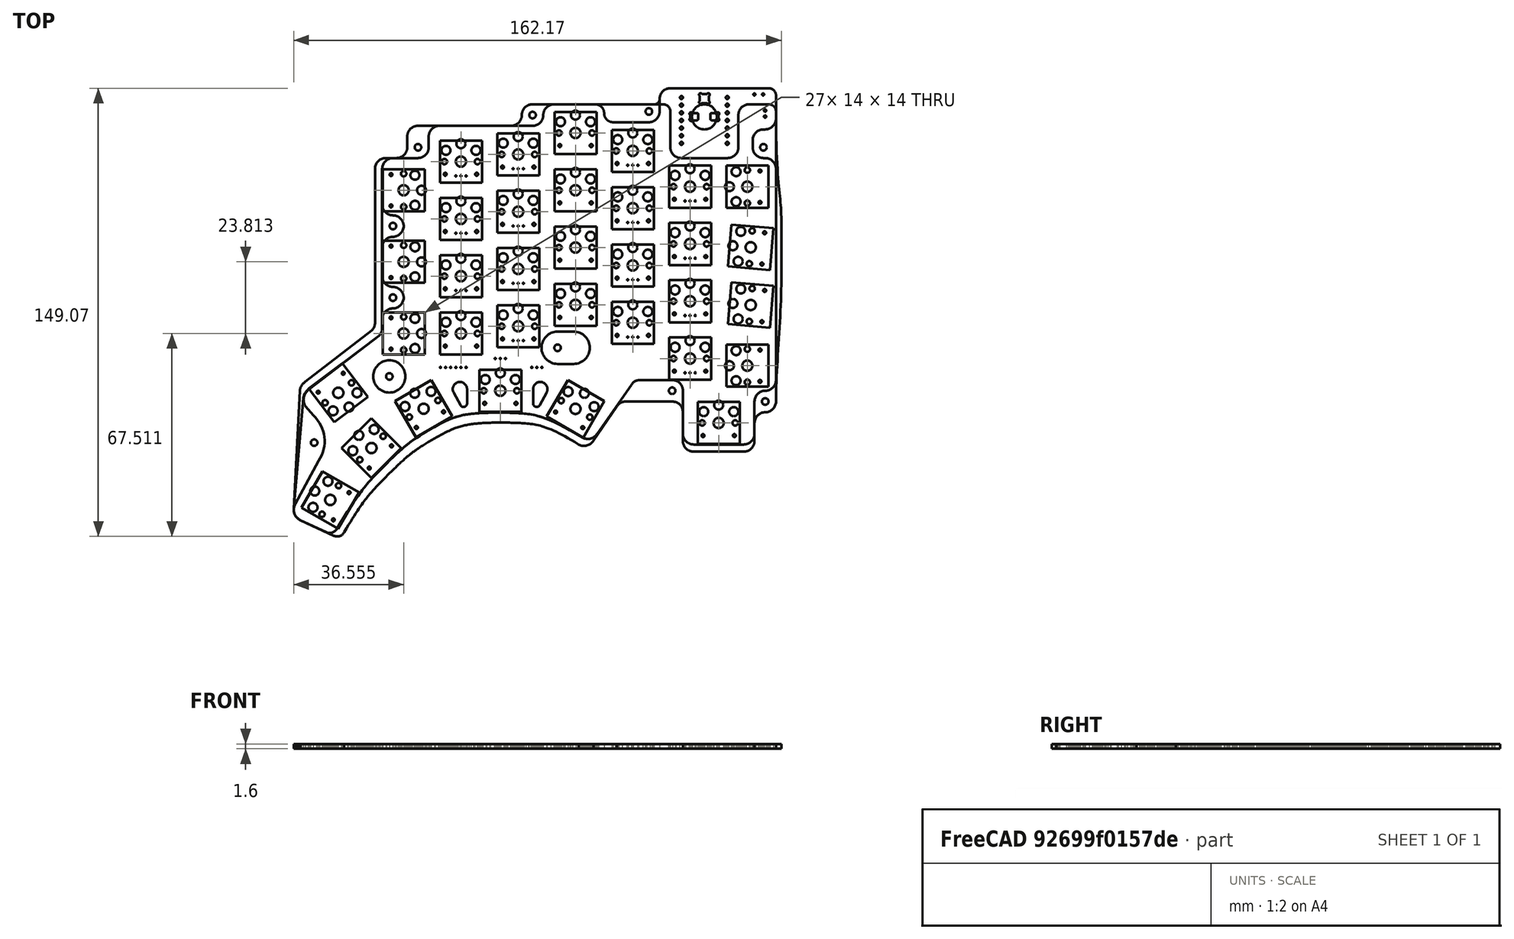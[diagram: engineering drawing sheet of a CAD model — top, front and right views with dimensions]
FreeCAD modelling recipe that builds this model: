
FCSTD DOCUMENT  (FreeCAD 0.20RUnknown)
Label: mykeeb_v7a3
License: All rights reserved
LicenseURL: http://en.wikipedia.org/wiki/All_rights_reserved
objects: App::Part×9, PartDesign::CoordinateSystem×3, Part::Feature×3, Sketcher::SketchObject×3
note: 9 computed .brp shape members not serialized (recipe doc carries the construction recipe); baked Part::Feature solids carry a one-line shape summary decoded from their .brp

FEATURE [PartDesign::CoordinateSystem] Local_CS_73e4
  AttacherType = Attacher::AttachEngine3D
  MapMode = 2
  Support = -> [X_Axis001]
FEATURE [Part::Feature] Pcb_73e4
  shape: bbox 160.4 x 147.9 x 1.6 mm, 455 faces (baked)
FEATURE [Sketcher::SketchObject] PCB_Sketch_73e4
  FullyConstrained = false
  sketch-geometry (120):
    g0: LineSegment StartX=214.313 StartY=-44.0531 StartZ=0 EndX=214.908 EndY=-44.0532 EndZ=0
    g1: LineSegment StartX=63.1589 StartY=-130.538 StartZ=0 EndX=86.4648 EndY=-112.659 EndZ=0
    g2: LineSegment StartX=218.48 StartY=-40.4812 StartZ=0 EndX=218.48 EndY=-32.7422 EndZ=0
    g3: LineSegment StartX=66.3691 StartY=-154.273 StartZ=0 EndX=58.6299 EndY=-168.63 EndZ=0
    g4: LineSegment StartX=159.033 StartY=-145.204 StartZ=0 EndX=170.339 EndY=-129.07 EndZ=0
    g5: LineSegment StartX=87.511 StartY=-92.8689 StartZ=0 EndX=87.511 EndY=-83.3438 EndZ=0
    g6: LineSegment StartX=60.2956 StartY=-173.994 StartZ=0 EndX=68.974 EndY=-178.03 EndZ=0
    g7: LineSegment StartX=216.099 StartY=-30.361 StartZ=0 EndX=183.356 EndY=-30.3609 EndZ=0
    g8: LineSegment StartX=191.095 StartY=-148.828 StartZ=0 EndX=207.764 EndY=-148.828 EndZ=0
    g9: LineSegment StartX=64.6194 StartY=-139.172 StartZ=0 EndX=62.0519 EndY=-136.234 EndZ=0
    g10: LineSegment StartX=218.48 StartY=-57.15 StartZ=0 EndX=218.48 EndY=-127.397 EndZ=0
    g11: LineSegment StartX=115.741 StartY=-130.425 StartZ=0 EndX=115.741 EndY=-135.187 EndZ=0
    g12: LineSegment StartX=187.524 StartY=-145.256 StartZ=0 EndX=187.524 EndY=-130.969 EndZ=0
    g13: LineSegment StartX=211.336 StartY=-145.256 StartZ=0 EndX=211.336 EndY=-134.541 EndZ=0
    g14: LineSegment StartX=87.511 StartY=-69.0563 StartZ=0 EndX=87.511 EndY=-57.15 EndZ=0
    g15: LineSegment StartX=99.4173 StartY=-53.5782 StartZ=0 EndX=91.0829 EndY=-53.5782 EndZ=0
    g16: LineSegment StartX=145.852 StartY=-122.039 StartZ=0 EndX=151.21 EndY=-122.039 EndZ=0
    g17: LineSegment StartX=137.717 StartY=-135.187 StartZ=0 EndX=137.717 EndY=-130.425 EndZ=0
    g18: LineSegment StartX=179.785 StartY=-38.1 StartZ=0 EndX=179.785 EndY=-33.9328 EndZ=0
    g19: LineSegment StartX=183.952 StartY=-127.397 StartZ=0 EndX=173.236 EndY=-127.397 EndZ=0
    g20: LineSegment StartX=106.561 StartY=-42.8625 StartZ=0 EndX=137.517 EndY=-42.8626 EndZ=0
    g21: LineSegment StartX=111.318 StartY=-131.65 StartZ=0 EndX=113.56 EndY=-135.848 EndZ=0
    g22: LineSegment StartX=210.741 StartY=-47.625 StartZ=0 EndX=210.741 EndY=-50.0063 EndZ=0
    g23: LineSegment StartX=214.313 StartY=-53.5782 StartZ=0 EndX=214.908 EndY=-53.5782 EndZ=0
    g24: LineSegment StartX=102.989 StartY=-50.0063 StartZ=0 EndX=102.989 EndY=-46.4344 EndZ=0
    g25: LineSegment StartX=164.307 StartY=-41.6719 StartZ=0 EndX=176.213 EndY=-41.6719 EndZ=0
    g26: LineSegment StartX=145.852 StartY=-111.324 StartZ=0 EndX=151.21 EndY=-111.324 EndZ=0
    g27: LineSegment StartX=144.661 StartY=-35.7187 StartZ=0 EndX=158.353 EndY=-35.7186 EndZ=0
    g28: LineSegment StartX=87.511 StartY=-107.156 StartZ=0 EndX=87.511 EndY=-110.133 EndZ=0
    g29: LineSegment StartX=139.899 StartY=-135.848 StartZ=0 EndX=142.14 EndY=-131.65 EndZ=0
    g30: BSplineCurve PolesCount=4 KnotsCount=2 Degree=3 IsPeriodic=0
    g31: BSplineCurve PolesCount=4 KnotsCount=2 Degree=3 IsPeriodic=0
    g32: BSplineCurve PolesCount=4 KnotsCount=2 Degree=3 IsPeriodic=0
    g33: BSplineCurve PolesCount=4 KnotsCount=2 Degree=3 IsPeriodic=0
    g34: BSplineCurve PolesCount=4 KnotsCount=2 Degree=3 IsPeriodic=0
    g35: BSplineCurve PolesCount=4 KnotsCount=2 Degree=3 IsPeriodic=0
    g36: BSplineCurve PolesCount=4 KnotsCount=2 Degree=3 IsPeriodic=0
    g37: ArcOfCircle CenterX=214.908 CenterY=-127.397 CenterZ=0 NormalX=0 NormalY=0 NormalZ=-1 AngleXU=3.14159 Radius=3.57183 StartAngle=0 EndAngle=1.57081
    g38: ArcOfCircle CenterX=183.356 CenterY=-33.9326 CenterZ=0 NormalX=0 NormalY=0 NormalZ=-1 AngleXU=-6.74926e-05 Radius=3.57168 StartAngle=0 EndAngle=1.57092
    g39: ArcOfCircle CenterX=138.908 CenterY=-135.187 CenterZ=0 NormalX=0 NormalY=0 NormalZ=-1 AngleXU=-2.55359 Radius=1.19063 StartAngle=0 EndAngle=2.55359
    g40: ArcOfCircle CenterX=191.095 CenterY=-145.257 CenterZ=0 NormalX=0 NormalY=0 NormalZ=-1 AngleXU=-1.57085 Radius=3.57175 StartAngle=0 EndAngle=1.57088
    g41: ArcOfCircle CenterX=151.21 CenterY=-116.681 CenterZ=0 NormalX=0 NormalY=0 NormalZ=-1 AngleXU=1.5708 Radius=5.35782 StartAngle=0 EndAngle=3.14159
    g42: ArcOfCircle CenterX=158.353 CenterY=-38.6953 CenterZ=0 NormalX=0 NormalY=0 NormalZ=-1 AngleXU=1.57078 Radius=2.97664 StartAngle=0 EndAngle=1.57081
    g43: ArcOfCircle CenterX=91.0829 CenterY=-83.3437 CenterZ=0 NormalX=0 NormalY=0 NormalZ=-1 AngleXU=-2.06565e-05 Radius=3.57185 StartAngle=0 EndAngle=1.57082
    g44: ArcOfCircle CenterX=83.9389 CenterY=-110.133 CenterZ=0 NormalX=0 NormalY=0 NormalZ=-1 AngleXU=-3.14156 Radius=3.5721 StartAngle=0 EndAngle=0.785347
    g45: ArcOfCircle CenterX=91.0829 CenterY=-107.156 CenterZ=0 NormalX=0 NormalY=0 NormalZ=-1 AngleXU=-1.82669e-05 Radius=3.57186 StartAngle=0 EndAngle=1.57082
    g46: ArcOfCircle CenterX=216.099 CenterY=-32.7422 CenterZ=0 NormalX=0 NormalY=0 NormalZ=-1 AngleXU=1.57078 Radius=2.38127 StartAngle=0 EndAngle=1.5708
    g47: ArcOfCircle CenterX=214.908 CenterY=-134.541 CenterZ=0 NormalX=0 NormalY=0 NormalZ=-1 AngleXU=2.28395e-06 Radius=3.57193 StartAngle=0 EndAngle=1.57078
    g48: ArcOfCircle CenterX=91.083 CenterY=-100.013 CenterZ=0 NormalX=0 NormalY=0 NormalZ=-1 AngleXU=1.57077 Radius=3.57181 StartAngle=1.31584e-05 EndAngle=1.57082
    g49: ArcOfCircle CenterX=183.952 CenterY=-130.969 CenterZ=0 NormalX=0 NormalY=0 NormalZ=-1 AngleXU=1.57077 Radius=3.57182 StartAngle=0 EndAngle=1.57084
    g50: ArcOfCircle CenterX=113.36 CenterY=-130.425 CenterZ=0 NormalX=0 NormalY=0 NormalZ=-1 AngleXU=-0.540421 Radius=2.38125 StartAngle=0 EndAngle=3.68201
    g51: ArcOfCircle CenterX=56.8441 CenterY=-147.725 CenterZ=0 NormalX=0 NormalY=0 NormalZ=-1 AngleXU=2.30861 Radius=11.5589 StartAngle=0 EndAngle=1.43527
    g52: ArcOfCircle CenterX=91.0829 CenterY=-76.2 CenterZ=0 NormalX=0 NormalY=0 NormalZ=-1 AngleXU=1.57078 Radius=3.57185 StartAngle=1.31581e-05 EndAngle=1.5708
    g53: ArcOfCircle CenterX=214.313 CenterY=-47.625 CenterZ=0 NormalX=0 NormalY=0 NormalZ=-1 AngleXU=-2.06565e-05 Radius=3.57185 StartAngle=0 EndAngle=1.57082
    g54: ArcOfCircle CenterX=91.0828 CenterY=-92.869 CenterZ=0 NormalX=0 NormalY=0 NormalZ=-1 AngleXU=-1.57083 Radius=3.5718 StartAngle=0 EndAngle=1.57085
    g55: ArcOfCircle CenterX=214.908 CenterY=-40.4813 CenterZ=0 NormalX=0 NormalY=0 NormalZ=-1 AngleXU=3.14157 Radius=3.57185 StartAngle=0 EndAngle=1.57083
    g56: ArcOfCircle CenterX=91.0829 CenterY=-76.2 CenterZ=0 NormalX=0 NormalY=0 NormalZ=-1 AngleXU=3.14157 Radius=3.57185 StartAngle=0 EndAngle=1.57082
    g57: ArcOfCircle CenterX=91.0829 CenterY=-100.013 CenterZ=0 NormalX=0 NormalY=0 NormalZ=-1 AngleXU=3.14157 Radius=3.57186 StartAngle=0 EndAngle=1.57082
    g58: ArcOfCircle CenterX=155.939 CenterY=-143.418 CenterZ=0 NormalX=0 NormalY=0 NormalZ=-1 AngleXU=-2.61789 Radius=3.57199 StartAngle=0 EndAngle=1.57071
    g59: ArcOfCircle CenterX=140.099 CenterY=-130.425 CenterZ=0 NormalX=0 NormalY=0 NormalZ=-1 AngleXU=5.56759e-08 Radius=2.38125 StartAngle=0 EndAngle=3.68201
    g60: ArcOfCircle CenterX=91.0829 CenterY=-57.15 CenterZ=0 NormalX=0 NormalY=0 NormalZ=-1 AngleXU=-8.07346e-07 Radius=3.57188 StartAngle=0 EndAngle=1.5708
    g61: ArcOfCircle CenterX=65.4842 CenterY=-133.945 CenterZ=0 NormalX=0 NormalY=0 NormalZ=-1 AngleXU=-0.588035 Radius=4.12518 StartAngle=0 EndAngle=1.55998
    g62: ArcOfCircle CenterX=164.306 CenterY=-38.6953 CenterZ=0 NormalX=0 NormalY=0 NormalZ=-1 AngleXU=-1.57083 Radius=2.9766 StartAngle=0 EndAngle=1.57084
    g63: ArcOfCircle CenterX=145.852 CenterY=-116.681 CenterZ=0 NormalX=0 NormalY=0 NormalZ=-1 AngleXU=-1.5708 Radius=5.35782 StartAngle=0 EndAngle=3.14159
    g64: ArcOfCircle CenterX=214.313 CenterY=-50.0063 CenterZ=0 NormalX=0 NormalY=0 NormalZ=-1 AngleXU=-1.57081 Radius=3.57187 StartAngle=0 EndAngle=1.57081
    g65: ArcOfCircle CenterX=173.236 CenterY=-130.743 CenterZ=0 NormalX=0 NormalY=0 NormalZ=-1 AngleXU=0.523591 Radius=3.34575 StartAngle=0 EndAngle=1.04722
    g66: ArcOfCircle CenterX=114.55 CenterY=-135.187 CenterZ=0 NormalX=0 NormalY=0 NormalZ=-1 AngleXU=3.14159 Radius=1.19063 StartAngle=0 EndAngle=2.55359
    g67: ArcOfCircle CenterX=106.561 CenterY=-46.4343 CenterZ=0 NormalX=0 NormalY=0 NormalZ=-1 AngleXU=-3.88176e-05 Radius=3.57179 StartAngle=0 EndAngle=1.57086
    g68: ArcOfCircle CenterX=61.8938 CenterY=-170.557 CenterZ=0 NormalX=0 NormalY=0 NormalZ=-1 AngleXU=-1.13553 Radius=3.79044 StartAngle=0 EndAngle=1.66889
    g69: ArcOfCircle CenterX=91.0828 CenterY=-69.0563 CenterZ=0 NormalX=0 NormalY=0 NormalZ=-1 AngleXU=-1.57082 Radius=3.57185 StartAngle=0 EndAngle=1.57082
    g70: ArcOfCircle CenterX=176.213 CenterY=-38.1001 CenterZ=0 NormalX=0 NormalY=0 NormalZ=-1 AngleXU=3.14158 Radius=3.57186 StartAngle=0 EndAngle=1.57082
    g71: ArcOfCircle CenterX=70.0798 CenterY=-175.652 CenterZ=0 NormalX=0 NormalY=0 NormalZ=-1 AngleXU=-2.69412 Radius=2.62232 StartAngle=0 EndAngle=1.55862
    g72: ArcOfCircle CenterX=214.908 CenterY=-57.15 CenterZ=0 NormalX=0 NormalY=0 NormalZ=-1 AngleXU=1.57078 Radius=3.57186 StartAngle=0 EndAngle=1.57082
    g73: ArcOfCircle CenterX=144.661 CenterY=-39.2905 CenterZ=0 NormalX=0 NormalY=0 NormalZ=-1 AngleXU=-5.07655e-05 Radius=3.57174 StartAngle=0 EndAngle=1.57088
    g74: ArcOfCircle CenterX=99.4174 CenterY=-50.0064 CenterZ=0 NormalX=0 NormalY=0 NormalZ=-1 AngleXU=3.14155 Radius=3.57178 StartAngle=0 EndAngle=1.57086
    g75: ArcOfCircle CenterX=137.517 CenterY=-39.2908 CenterZ=0 NormalX=0 NormalY=0 NormalZ=-1 AngleXU=3.14156 Radius=3.57181 StartAngle=0 EndAngle=1.57085
    g76: ArcOfCircle CenterX=207.764 CenterY=-145.257 CenterZ=0 NormalX=0 NormalY=0 NormalZ=-1 AngleXU=3.14156 Radius=3.57181 StartAngle=0 EndAngle=1.57085
    g77: Circle CenterX=89.8922 CenterY=-126.206 CenterZ=0 NormalX=0 NormalY=0 NormalZ=1 AngleXU=0 Radius=5.35782
    g78-g81: Circle x4 (B-spline internal-alignment scaffolding for g30; pole/knot coordinates omitted)
    g82: GeomPoint X=84.5515 Y=-159.708 Z=0
    g83: GeomPoint X=72.4439 Y=-176.787 Z=0
    g84-g87: Circle x4 (B-spline internal-alignment scaffolding for g31; pole/knot coordinates omitted)
    g88: GeomPoint X=99.9796 Y=-145.916 Z=0
    g89: GeomPoint X=93.1338 Y=-151.175 Z=0
    g90-g93: Circle x4 (B-spline internal-alignment scaffolding for g32; pole/knot coordinates omitted)
    g94: GeomPoint X=110.199 Y=-140.36 Z=0
    g95: GeomPoint X=99.9796 Y=-145.916 Z=0
    g96-g99: Circle x4 (B-spline internal-alignment scaffolding for g33; pole/knot coordinates omitted)
    g100: GeomPoint X=154.153 Y=-146.511 Z=0
    g101: GeomPoint X=133.615 Y=-138.475 Z=0
    g102-g105: Circle x4 (B-spline internal-alignment scaffolding for g34; pole/knot coordinates omitted)
    g106: GeomPoint X=120.518 Y=-138.376 Z=0
    g107: GeomPoint X=110.199 Y=-140.36 Z=0
    g108-g111: Circle x4 (B-spline internal-alignment scaffolding for g35; pole/knot coordinates omitted)
    g112: GeomPoint X=93.1338 Y=-151.175 Z=0
    g113: GeomPoint X=84.5515 Y=-159.708 Z=0
    g114-g117: Circle x4 (B-spline internal-alignment scaffolding for g36; pole/knot coordinates omitted)
    g118: GeomPoint X=133.615 Y=-138.475 Z=0
    g119: GeomPoint X=120.518 Y=-138.376 Z=0
  constraints (84):
    c: Coincident(g3,g68)
    c: Coincident(g6,g68)
    c: Coincident(g9,g61)
    c: Coincident(g1,g61)
    c: Coincident(g9,g51)
    c: Coincident(g3,g51)
    c: Coincident(g6,g71)
    c: Coincident(g30,g71)
    c: Coincident(g30,g35)
    c: Coincident(g1,g44)
    c: Coincident(g28,g44)
    c: Coincident(g28,g45)
    c: Coincident(g5,g54)
    c: Coincident(g5,g43)
    c: Coincident(g14,g69)
    c: Coincident(g14,g60)
    c: Coincident(g45,g57)
    c: Coincident(g48,g54)
    c: Coincident(g43,g56)
    c: Coincident(g52,g69)
    c: Coincident(g15,g60)
    c: Coincident(g31,g35)
    c: Coincident(g48,g57)
    c: Coincident(g52,g56)
    c: Coincident(g15,g74)
    c: Coincident(g31,g32)
    c: Coincident(g24,g74)
    c: Coincident(g24,g67)
    c: Coincident(g20,g67)
    c: Coincident(g32,g34)
    c: Coincident(g21,g50)
    c: Coincident(g21,g66)
    c: Coincident(g11,g66)
    c: Coincident(g11,g50)
    c: Coincident(g34,g36)
    c: Coincident(g33,g36)
    c: Coincident(g20,g75)
    c: Coincident(g17,g39)
    c: Coincident(g17,g59)
    c: Coincident(g29,g39)
    c: Coincident(g73,g75)
    c: Coincident(g29,g59)
    c: Coincident(g27,g73)
    c: Coincident(g16,g63)
    c: Coincident(g26,g63)
    c: Coincident(g16,g41)
    c: Coincident(g26,g41)
    c: Coincident(g33,g58)
    c: Coincident(g27,g42)
    c: Coincident(g4,g58)
    c: Coincident(g42,g62)
    c: Coincident(g25,g62)
    c: Coincident(g4,g65)
    c: Coincident(g19,g65)
    c: Coincident(g25,g70)
    c: Coincident(g18,g70)
    c: Coincident(g18,g38)
    c: Coincident(g7,g38)
    c: Coincident(g19,g49)
    c: Coincident(g12,g40)
    c: Coincident(g12,g49)
    c: Coincident(g8,g40)
    c: Coincident(g8,g76)
    c: Coincident(g22,g64)
    c: Coincident(g22,g53)
    c: Coincident(g13,g76)
    c: Coincident(g13,g47)
    c: Coincident(g23,g64)
    c: Coincident(g0,g53)
    c: Coincident(g37,g47)
    c: Coincident(g23,g72)
    c: Coincident(g0,g55)
    c: Coincident(g7,g46)
    c: Coincident(g10,g37)
    c: Coincident(g10,g72)
    c: Coincident(g2,g55)
    c: Coincident(g2,g46)
    c: InternalAlignment(g78-g83 -> g30) x6
    c: InternalAlignment(g84-g89 -> g31) x6
    c: InternalAlignment(g90-g95 -> g32) x6
    c: InternalAlignment(g96-g101 -> g33) x6
    c: InternalAlignment(g102-g107 -> g34) x6
    c: InternalAlignment(g108-g113 -> g35) x6
    c: InternalAlignment(g114-g119 -> g36) x6
FEATURE [App::Part] Board_Geoms_73e4
  Group = -> [Pcb_73e4,PCB_Sketch_73e4]
  Origin = -> Origin
FEATURE [App::Part] Step_Models_73e4
  Origin = -> Origin002
FEATURE [App::Part] Board_73e4  label="mykeeb_v7a3"
  Group = -> [Local_CS_73e4,Board_Geoms_73e4,Step_Models_73e4]
  Origin = -> Origin001
FEATURE [PartDesign::CoordinateSystem] Local_CS_1d9e
  AttacherType = Attacher::AttachEngine3D
  MapMode = 2
  Support = -> [X_Axis003]
FEATURE [Part::Feature] Pcb_1d9e
  shape: bbox 162.2 x 143.7 x 1.6 mm, 205 faces (baked)
FEATURE [Sketcher::SketchObject] PCB_Sketch_1d9e
  FullyConstrained = false
  sketch-geometry (110):
    g0: LineSegment StartX=209.55 StartY=-35.7188 StartZ=0 EndX=216.099 EndY=-35.7188 EndZ=0
    g1: LineSegment StartX=61.9126 StartY=-127.992 StartZ=0 EndX=84.0836 EndY=-110.873 EndZ=0
    g2: LineSegment StartX=183.357 StartY=-50.0061 StartZ=0 EndX=183.356 EndY=-38.1 EndZ=0
    g3: LineSegment StartX=60.1315 StartY=-130.976 StartZ=0 EndX=58.1131 EndY=-170.286 EndZ=0
    g4: LineSegment StartX=157.758 StartY=-147.521 StartZ=0 EndX=165.576 EndY=-136.214 EndZ=0
    g5: LineSegment StartX=60.2956 StartY=-173.994 StartZ=0 EndX=71.4376 EndY=-179.189 EndZ=0
    g6: LineSegment StartX=202.406 StartY=-53.5782 StartZ=0 EndX=186.929 EndY=-53.578 EndZ=0
    g7: LineSegment StartX=191.095 StartY=-151.21 StartZ=0 EndX=207.764 EndY=-151.21 EndZ=0
    g8: LineSegment StartX=220.266 StartY=-74.4141 StartZ=0 EndX=220.266 EndY=-94.0595 EndZ=0
    g9: LineSegment StartX=115.741 StartY=-130.425 StartZ=0 EndX=115.741 EndY=-135.187 EndZ=0
    g10: LineSegment StartX=187.524 StartY=-147.638 StartZ=0 EndX=187.524 EndY=-138.113 EndZ=0
    g11: LineSegment StartX=211.336 StartY=-147.638 StartZ=0 EndX=211.336 EndY=-141.684 EndZ=0
    g12: LineSegment StartX=92.2735 StartY=-53.5782 StartZ=0 EndX=88.7016 EndY=-53.5782 EndZ=0
    g13: LineSegment StartX=137.717 StartY=-135.187 StartZ=0 EndX=137.717 EndY=-130.425 EndZ=0
    g14: LineSegment StartX=183.952 StartY=-134.541 StartZ=0 EndX=168.474 EndY=-134.541 EndZ=0
    g15: LineSegment StartX=99.4173 StartY=-42.8625 StartZ=0 EndX=130.374 EndY=-42.8626 EndZ=0
    g16: LineSegment StartX=111.318 StartY=-131.65 StartZ=0 EndX=113.56 EndY=-135.848 EndZ=0
    g17: LineSegment StartX=205.978 StartY=-39.2907 StartZ=0 EndX=205.978 EndY=-50.0063 EndZ=0
    g18: LineSegment StartX=95.8454 StartY=-50.0062 StartZ=0 EndX=95.8454 EndY=-46.4344 EndZ=0
    g19: LineSegment StartX=137.517 StartY=-35.7188 StartZ=0 EndX=180.975 EndY=-35.7188 EndZ=0
    g20: LineSegment StartX=85.1298 StartY=-57.15 StartZ=0 EndX=85.1298 EndY=-108.347 EndZ=0
    g21: LineSegment StartX=139.899 StartY=-135.848 StartZ=0 EndX=142.14 EndY=-131.65 EndZ=0
    g22: BSplineCurve PolesCount=4 KnotsCount=2 Degree=3 IsPeriodic=0
    g23: BSplineCurve PolesCount=4 KnotsCount=2 Degree=3 IsPeriodic=0
    g24: BSplineCurve PolesCount=4 KnotsCount=2 Degree=3 IsPeriodic=0
    g25: BSplineCurve PolesCount=4 KnotsCount=2 Degree=3 IsPeriodic=0
    g26: BSplineCurve PolesCount=4 KnotsCount=2 Degree=3 IsPeriodic=0
    g27: BSplineCurve PolesCount=4 KnotsCount=2 Degree=3 IsPeriodic=0
    g28: BSplineCurve PolesCount=4 KnotsCount=2 Degree=3 IsPeriodic=0
    g29: BSplineCurve PolesCount=4 KnotsCount=2 Degree=3 IsPeriodic=0
    g30: BSplineCurve PolesCount=4 KnotsCount=2 Degree=3 IsPeriodic=0
    g31: ArcOfCircle CenterX=214.908 CenterY=-134.541 CenterZ=0 NormalX=0 NormalY=0 NormalZ=-1 AngleXU=-3.14158 Radius=3.57189 StartAngle=0 EndAngle=1.57078
    g32: ArcOfCircle CenterX=186.928 CenterY=-50.0063 CenterZ=0 NormalX=0 NormalY=0 NormalZ=-1 AngleXU=-1.57086 Radius=3.57169 StartAngle=0 EndAngle=1.57091
    g33: ArcOfCircle CenterX=138.908 CenterY=-135.187 CenterZ=0 NormalX=0 NormalY=0 NormalZ=-1 AngleXU=-2.55359 Radius=1.19063 StartAngle=0 EndAngle=2.55359
    g34: ArcOfCircle CenterX=191.095 CenterY=-147.638 CenterZ=0 NormalX=0 NormalY=0 NormalZ=-1 AngleXU=-1.57084 Radius=3.57178 StartAngle=0 EndAngle=1.57086
    g35: ArcOfCircle CenterX=81.5576 CenterY=-108.347 CenterZ=0 NormalX=0 NormalY=0 NormalZ=-1 AngleXU=-3.14155 Radius=3.57218 StartAngle=0 EndAngle=0.785329
    g36: ArcOfCircle CenterX=180.975 CenterY=-38.1001 CenterZ=0 NormalX=0 NormalY=0 NormalZ=-1 AngleXU=1.57079 Radius=2.38129 StartAngle=0 EndAngle=1.57078
    g37: ArcOfCircle CenterX=214.908 CenterY=-141.685 CenterZ=0 NormalX=0 NormalY=0 NormalZ=-1 AngleXU=6.10736e-06 Radius=3.57195 StartAngle=0 EndAngle=1.57077
    g38: ArcOfCircle CenterX=183.952 CenterY=-138.113 CenterZ=0 NormalX=0 NormalY=0 NormalZ=-1 AngleXU=1.57079 Radius=3.57192 StartAngle=0 EndAngle=1.57079
    g39: ArcOfCircle CenterX=113.36 CenterY=-130.425 CenterZ=0 NormalX=0 NormalY=0 NormalZ=-1 AngleXU=-0.540421 Radius=2.38125 StartAngle=0 EndAngle=3.68201
    g40: ArcOfCircle CenterX=209.55 CenterY=-39.2906 CenterZ=0 NormalX=0 NormalY=0 NormalZ=-1 AngleXU=-1.39656e-05 Radius=3.57188 StartAngle=0 EndAngle=1.57081
    g41: ArcOfCircle CenterX=154.665 CenterY=-145.735 CenterZ=0 NormalX=0 NormalY=0 NormalZ=-1 AngleXU=-2.61787 Radius=3.57207 StartAngle=0 EndAngle=1.57066
    g42: ArcOfCircle CenterX=140.099 CenterY=-130.425 CenterZ=0 NormalX=0 NormalY=0 NormalZ=-1 AngleXU=5.56759e-08 Radius=2.38125 StartAngle=0 EndAngle=3.68201
    g43: ArcOfCircle CenterX=88.7016 CenterY=-57.15 CenterZ=0 NormalX=0 NormalY=0 NormalZ=-1 AngleXU=-1.75348e-05 Radius=3.57182 StartAngle=0 EndAngle=1.57083
    g44: ArcOfCircle CenterX=64.2427 CenterY=-131.407 CenterZ=0 NormalX=0 NormalY=0 NormalZ=-1 AngleXU=0.104395 Radius=4.13378 StartAngle=0 EndAngle=0.867549
    g45: ArcOfCircle CenterX=202.406 CenterY=-50.0064 CenterZ=0 NormalX=0 NormalY=0 NormalZ=-1 AngleXU=3.14157 Radius=3.57184 StartAngle=0 EndAngle=1.57083
    g46: ArcOfCircle CenterX=168.474 CenterY=-137.887 CenterZ=0 NormalX=0 NormalY=0 NormalZ=-1 AngleXU=0.523599 Radius=3.3458 StartAngle=0 EndAngle=1.0472
    g47: ArcOfCircle CenterX=114.55 CenterY=-135.187 CenterZ=0 NormalX=0 NormalY=0 NormalZ=-1 AngleXU=3.14159 Radius=1.19063 StartAngle=0 EndAngle=2.55359
    g48: ArcOfCircle CenterX=99.4172 CenterY=-46.4343 CenterZ=0 NormalX=0 NormalY=0 NormalZ=-1 AngleXU=-3.49942e-05 Radius=3.5718 StartAngle=0 EndAngle=1.57085
    g49: ArcOfCircle CenterX=61.8938 CenterY=-170.557 CenterZ=0 NormalX=0 NormalY=0 NormalZ=-1 AngleXU=-1.13554 Radius=3.79043 StartAngle=0 EndAngle=1.20715
    g50: ArcOfCircle CenterX=72.5433 CenterY=-176.811 CenterZ=0 NormalX=0 NormalY=0 NormalZ=-1 AngleXU=-2.69413 Radius=2.62229 StartAngle=0 EndAngle=1.55864
    g51: ArcOfCircle CenterX=216.099 CenterY=-38.1 CenterZ=0 NormalX=0 NormalY=0 NormalZ=-1 AngleXU=1.57078 Radius=2.38125 StartAngle=0 EndAngle=1.57083
    g52: ArcOfCircle CenterX=137.517 CenterY=-39.2906 CenterZ=0 NormalX=0 NormalY=0 NormalZ=-1 AngleXU=-2.73475e-05 Radius=3.57183 StartAngle=0 EndAngle=1.57084
    g53: ArcOfCircle CenterX=92.2736 CenterY=-50.0063 CenterZ=0 NormalX=0 NormalY=0 NormalZ=-1 AngleXU=3.14157 Radius=3.57184 StartAngle=0 EndAngle=1.57083
    g54: ArcOfCircle CenterX=130.374 CenterY=-39.2909 CenterZ=0 NormalX=0 NormalY=0 NormalZ=-1 AngleXU=3.14155 Radius=3.57176 StartAngle=0 EndAngle=1.57088
    g55: ArcOfCircle CenterX=207.764 CenterY=-147.638 CenterZ=0 NormalX=0 NormalY=0 NormalZ=-1 AngleXU=3.14158 Radius=3.57186 StartAngle=0 EndAngle=1.57082
    g56-g59: Circle x4 (B-spline internal-alignment scaffolding for g22; pole/knot coordinates omitted)
    g60: GeomPoint X=85.4774 Y=-163.017 Z=0
    g61: GeomPoint X=74.9075 Y=-177.946 Z=0
    g62-g65: Circle x4 (B-spline internal-alignment scaffolding for g23; pole/knot coordinates omitted)
    g66: GeomPoint X=100.906 Y=-149.225 Z=0
    g67: GeomPoint X=94.0597 Y=-154.483 Z=0
    g68-g71: Circle x4 (B-spline internal-alignment scaffolding for g24; pole/knot coordinates omitted)
    g72: GeomPoint X=220.266 Y=-94.0595 Z=0
    g73: GeomPoint X=218.48 Y=-134.541 Z=0
    g74-g77: Circle x4 (B-spline internal-alignment scaffolding for g25; pole/knot coordinates omitted)
    g78: GeomPoint X=111.125 Y=-143.669 Z=0
    g79: GeomPoint X=100.906 Y=-149.225 Z=0
    g80-g83: Circle x4 (B-spline internal-alignment scaffolding for g26; pole/knot coordinates omitted)
    g84: GeomPoint X=152.879 Y=-148.828 Z=0
    g85: GeomPoint X=134.541 Y=-141.784 Z=0
    g86-g89: Circle x4 (B-spline internal-alignment scaffolding for g27; pole/knot coordinates omitted)
    g90: GeomPoint X=121.444 Y=-141.684 Z=0
    g91: GeomPoint X=111.125 Y=-143.669 Z=0
    g92-g95: Circle x4 (B-spline internal-alignment scaffolding for g28; pole/knot coordinates omitted)
    g96: GeomPoint X=94.0597 Y=-154.483 Z=0
    g97: GeomPoint X=85.4774 Y=-163.017 Z=0
    g98-g101: Circle x4 (B-spline internal-alignment scaffolding for g29; pole/knot coordinates omitted)
    g102: GeomPoint X=134.541 Y=-141.784 Z=0
    g103: GeomPoint X=121.444 Y=-141.684 Z=0
    g104-g107: Circle x4 (B-spline internal-alignment scaffolding for g30; pole/knot coordinates omitted)
    g108: GeomPoint X=218.48 Y=-38.1001 Z=0
    g109: GeomPoint X=220.266 Y=-74.4141 Z=0
  constraints (65):
    c: Coincident(g3,g49)
    c: Coincident(g3,g44)
    c: Coincident(g5,g49)
    c: Coincident(g1,g44)
    c: Coincident(g5,g50)
    c: Coincident(g22,g50)
    c: Coincident(g1,g35)
    c: Coincident(g20,g35)
    c: Coincident(g20,g43)
    c: Coincident(g22,g28)
    c: Coincident(g12,g43)
    c: Coincident(g12,g53)
    c: Coincident(g23,g28)
    c: Coincident(g18,g53)
    c: Coincident(g18,g48)
    c: Coincident(g15,g48)
    c: Coincident(g23,g25)
    c: Coincident(g25,g27)
    c: Coincident(g16,g39)
    c: Coincident(g16,g47)
    c: Coincident(g9,g47)
    c: Coincident(g9,g39)
    c: Coincident(g27,g29)
    c: Coincident(g15,g54)
    c: Coincident(g52,g54)
    c: Coincident(g26,g29)
    c: Coincident(g19,g52)
    c: Coincident(g13,g33)
    c: Coincident(g13,g42)
    c: Coincident(g21,g33)
    c: Coincident(g21,g42)
    c: Coincident(g26,g41)
    c: Coincident(g4,g41)
    c: Coincident(g4,g46)
    c: Coincident(g14,g46)
    c: Coincident(g19,g36)
    c: Coincident(g2,g32)
    c: Coincident(g2,g36)
    c: Coincident(g14,g38)
    c: Coincident(g6,g32)
    c: Coincident(g10,g34)
    c: Coincident(g10,g38)
    c: Coincident(g7,g34)
    c: Coincident(g6,g45)
    c: Coincident(g17,g45)
    c: Coincident(g17,g40)
    c: Coincident(g7,g55)
    c: Coincident(g0,g40)
    c: Coincident(g11,g55)
    c: Coincident(g11,g37)
    c: Coincident(g31,g37)
    c: Coincident(g0,g51)
    c: Coincident(g24,g31)
    c: Coincident(g30,g51)
    c: Coincident(g8,g24)
    c: Coincident(g8,g30)
    c: InternalAlignment(g56-g61 -> g22) x6
    c: InternalAlignment(g62-g67 -> g23) x6
    c: InternalAlignment(g68-g73 -> g24) x6
    c: InternalAlignment(g74-g79 -> g25) x6
    c: InternalAlignment(g80-g85 -> g26) x6
    c: InternalAlignment(g86-g91 -> g27) x6
    c: InternalAlignment(g92-g97 -> g28) x6
    c: InternalAlignment(g98-g103 -> g29) x6
    c: InternalAlignment(g104-g109 -> g30) x6
FEATURE [App::Part] Board_Geoms_1d9e
  Group = -> [Pcb_1d9e,PCB_Sketch_1d9e]
  Origin = -> Origin004
FEATURE [App::Part] Step_Models_1d9e
  Origin = -> Origin005
FEATURE [App::Part] Board_1d9e  label="mykeeb_v7a3-plate"
  Group = -> [Local_CS_1d9e,Board_Geoms_1d9e,Step_Models_1d9e]
  Origin = -> Origin003
  Placement = pos=(0,0,3) rot=(0,0,1;0rad)
FEATURE [PartDesign::CoordinateSystem] Local_CS_ed69
  AttacherType = Attacher::AttachEngine3D
  MapMode = 2
  Support = -> [X_Axis006]
FEATURE [Part::Feature] Pcb_ed69
  shape: bbox 160.4 x 147.9 x 1.6 mm, 214 faces (baked)
FEATURE [Sketcher::SketchObject] PCB_Sketch_ed69
  FullyConstrained = false
  sketch-geometry (201):
    g0: LineSegment StartX=70.3558 StartY=-178.26 StartZ=0 EndX=70.4802 EndY=-178.244 EndZ=0
    g1: LineSegment StartX=92.1648 StartY=-152.078 StartZ=0 EndX=91.1301 EndY=-153.066 EndZ=0
    g2: LineSegment StartX=154.813 StartY=-146.808 StartZ=0 EndX=154.983 EndY=-146.86 EndZ=0
    g3: LineSegment StartX=59.0398 StartY=-173.052 StartZ=0 EndX=59.1728 EndY=-173.196 EndZ=0
    g4: LineSegment StartX=157.349 StartY=-146.7 StartZ=0 EndX=157.506 EndY=-146.628 EndZ=0
    g5: LineSegment StartX=122.009 StartY=-138.311 StartZ=0 EndX=120.518 EndY=-138.376 EndZ=0
    g6: LineSegment StartX=70.6034 StartY=-178.222 StartZ=0 EndX=70.7253 EndY=-178.194 EndZ=0
    g7: LineSegment StartX=146.549 StartY=-142.284 StartZ=0 EndX=145.013 EndY=-141.542 EndZ=0
    g8: LineSegment StartX=59.9431 StartY=-173.807 StartZ=0 EndX=60.1164 EndY=-173.905 EndZ=0
    g9: LineSegment StartX=69.7244 StartY=-178.251 StartZ=0 EndX=69.8513 EndY=-178.265 EndZ=0
    g10: LineSegment StartX=155.498 StartY=-146.963 StartZ=0 EndX=155.67 EndY=-146.98 EndZ=0
    g11: LineSegment StartX=97.2466 StartY=-147.763 StartZ=0 EndX=96.445 EndY=-148.359 EndZ=0
    g12: LineSegment StartX=77.9349 StartY=-168.167 StartZ=0 EndX=77.0295 EndY=-169.536 EndZ=0
    g13: LineSegment StartX=123.569 StartY=-138.265 StartZ=0 EndX=122.009 EndY=-138.311 EndZ=0
    g14: LineSegment StartX=93.1338 StartY=-151.175 StartZ=0 EndX=92.1648 EndY=-152.078 EndZ=0
    g15: LineSegment StartX=106.172 StartY=-142.257 StartZ=0 EndX=104.829 EndY=-142.989 EndZ=0
    g16: LineSegment StartX=155.325 StartY=-146.937 StartZ=0 EndX=155.498 EndY=-146.963 EndZ=0
    g17: LineSegment StartX=116.468 StartY=-138.724 StartZ=0 EndX=115.21 EndY=-138.921 EndZ=0
    g18: LineSegment StartX=131.929 StartY=-138.377 StartZ=0 EndX=130.229 EndY=-138.306 EndZ=0
    g19: LineSegment StartX=157.808 StartY=-146.463 StartZ=0 EndX=157.953 EndY=-146.369 EndZ=0
    g20: LineSegment StartX=154.315 StartY=-146.599 StartZ=0 EndX=154.479 EndY=-146.678 EndZ=0
    g21: LineSegment StartX=60.1164 StartY=-173.905 StartZ=0 EndX=60.2955 EndY=-173.994 EndZ=0
    g22: LineSegment StartX=69.2207 StartY=-178.13 StartZ=0 EndX=69.3457 EndY=-178.17 EndZ=0
    g23: LineSegment StartX=108.877 StartY=-140.924 StartZ=0 EndX=107.528 EndY=-141.563 EndZ=0
    g24: LineSegment StartX=58.1566 StartY=-169.924 StartZ=0 EndX=58.1288 EndY=-170.118 EndZ=0
    g25: LineSegment StartX=183.356 StartY=-30.361 StartZ=0 EndX=216.099 EndY=-30.3609 EndZ=0
    g26: LineSegment StartX=70.4802 StartY=-178.244 StartZ=0 EndX=70.6034 EndY=-178.222 EndZ=0
    g27: LineSegment StartX=58.7971 StartY=-172.743 StartZ=0 EndX=58.9145 EndY=-172.901 EndZ=0
    g28: LineSegment StartX=63.1032 StartY=-130.374 StartZ=0 EndX=86.4648 EndY=-112.659 EndZ=0
    g29: LineSegment StartX=71.5227 StartY=-177.842 StartZ=0 EndX=71.626 EndY=-177.771 EndZ=0
    g30: LineSegment StartX=59.3132 StartY=-173.333 StartZ=0 EndX=59.4606 EndY=-173.464 EndZ=0
    g31: LineSegment StartX=139.977 StartY=-139.56 StartZ=0 EndX=138.936 EndY=-139.265 EndZ=0
    g32: LineSegment StartX=156.529 StartY=-146.941 StartZ=0 EndX=156.697 EndY=-146.908 EndZ=0
    g33: LineSegment StartX=71.7261 StartY=-177.694 StartZ=0 EndX=71.8227 EndY=-177.612 EndZ=0
    g34: LineSegment StartX=58.6879 StartY=-172.58 StartZ=0 EndX=58.7971 EndY=-172.743 EndZ=0
    g35: LineSegment StartX=155.153 StartY=-146.903 StartZ=0 EndX=155.325 EndY=-146.937 EndZ=0
    g36: LineSegment StartX=76.0363 StartY=-171.068 StartZ=0 EndX=74.9467 EndY=-172.777 EndZ=0
    g37: LineSegment StartX=99.9796 StartY=-145.916 StartZ=0 EndX=98.9895 EndY=-146.561 EndZ=0
    g38: LineSegment StartX=110.845 StartY=-140.111 StartZ=0 EndX=110.199 EndY=-140.36 EndZ=0
    g39: LineSegment StartX=74.9467 StartY=-172.777 StartZ=0 EndX=73.7521 EndY=-174.679 EndZ=0
    g40: LineSegment StartX=80.8499 StartY=-164.031 StartZ=0 EndX=80.21 EndY=-164.893 EndZ=0
    g41: LineSegment StartX=71.9156 StartY=-177.525 StartZ=0 EndX=72.0045 EndY=-177.434 EndZ=0
    g42: LineSegment StartX=58.1062 StartY=-170.706 StartZ=0 EndX=58.1191 EndY=-170.903 EndZ=0
    g43: LineSegment StartX=71.307 StartY=-177.97 StartZ=0 EndX=71.4163 EndY=-177.908 EndZ=0
    g44: LineSegment StartX=154.153 StartY=-146.511 StartZ=0 EndX=154.315 EndY=-146.599 EndZ=0
    g45: LineSegment StartX=58.1288 StartY=-170.118 StartZ=0 EndX=58.1111 EndY=-170.313 EndZ=0
    g46: LineSegment StartX=142.297 StartY=-140.372 StartZ=0 EndX=141.094 EndY=-139.926 EndZ=0
    g47: LineSegment StartX=69.0967 StartY=-178.083 StartZ=0 EndX=69.2207 EndY=-178.13 EndZ=0
    g48: LineSegment StartX=59.4606 StartY=-173.464 StartZ=0 EndX=59.615 EndY=-173.586 EndZ=0
    g49: LineSegment StartX=126.843 StartY=-138.239 StartZ=0 EndX=125.185 EndY=-138.241 EndZ=0
    g50: LineSegment StartX=59.615 StartY=-173.586 StartZ=0 EndX=59.7759 EndY=-173.701 EndZ=0
    g51: LineSegment StartX=128.529 StartY=-138.26 StartZ=0 EndX=126.843 EndY=-138.239 EndZ=0
    g52: LineSegment StartX=61.3221 StartY=-133.357 StartZ=0 EndX=58.1566 EndY=-169.924 EndZ=0
    g53: LineSegment StartX=59.1728 StartY=-173.196 StartZ=0 EndX=59.3132 EndY=-173.333 EndZ=0
    g54: LineSegment StartX=70.7253 StartY=-178.194 StartZ=0 EndX=70.8457 EndY=-178.16 EndZ=0
    g55: LineSegment StartX=58.1036 StartY=-170.51 StartZ=0 EndX=58.1062 EndY=-170.706 EndZ=0
    g56: LineSegment StartX=72.2457 StartY=-177.131 StartZ=0 EndX=72.3169 EndY=-177.021 EndZ=0
    g57: LineSegment StartX=58.9145 StartY=-172.901 StartZ=0 EndX=59.0398 EndY=-173.052 EndZ=0
    g58: LineSegment StartX=159.033 StartY=-145.204 StartZ=0 EndX=165.576 EndY=-136.214 EndZ=0
    g59: LineSegment StartX=94.8591 StartY=-149.641 StartZ=0 EndX=94.0261 EndY=-150.367 EndZ=0
    g60: LineSegment StartX=69.5977 StartY=-178.23 StartZ=0 EndX=69.7244 EndY=-178.251 EndZ=0
    g61: LineSegment StartX=158.231 StartY=-146.159 StartZ=0 EndX=158.362 EndY=-146.043 EndZ=0
    g62: LineSegment StartX=73.7521 StartY=-174.679 StartZ=0 EndX=72.4439 EndY=-176.787 EndZ=0
    g63: LineSegment StartX=150.035 StartY=-144.127 StartZ=0 EndX=148.219 EndY=-143.142 EndZ=0
    g64: LineSegment StartX=156.016 StartY=-146.989 StartZ=0 EndX=156.188 EndY=-146.981 EndZ=0
    g65: LineSegment StartX=81.4449 StartY=-163.259 StartZ=0 EndX=80.8499 EndY=-164.031 EndZ=0
    g66: LineSegment StartX=103.518 StartY=-143.739 StartZ=0 EndX=102.26 EndY=-144.49 EndZ=0
    g67: LineSegment StartX=158.362 StartY=-146.043 StartZ=0 EndX=158.489 EndY=-145.921 EndZ=0
    g68: LineSegment StartX=72.1698 StartY=-177.237 StartZ=0 EndX=72.2457 EndY=-177.131 EndZ=0
    g69: LineSegment StartX=156.359 StartY=-146.965 StartZ=0 EndX=156.529 EndY=-146.941 EndZ=0
    g70: LineSegment StartX=82.5343 StartY=-161.928 StartZ=0 EndX=82.0035 EndY=-162.563 EndZ=0
    g71: LineSegment StartX=156.864 StartY=-146.868 StartZ=0 EndX=157.028 EndY=-146.82 EndZ=0
    g72: LineSegment StartX=58.3381 StartY=-171.871 StartZ=0 EndX=58.412 EndY=-172.055 EndZ=0
    g73: LineSegment StartX=191.095 StartY=-148.828 StartZ=0 EndX=207.764 EndY=-148.828 EndZ=0
    g74: LineSegment StartX=158.725 StartY=-145.654 StartZ=0 EndX=158.834 EndY=-145.511 EndZ=0
    g75: LineSegment StartX=71.1951 StartY=-178.025 StartZ=0 EndX=71.307 EndY=-177.97 EndZ=0
    g76: LineSegment StartX=72.0045 StartY=-177.434 StartZ=0 EndX=72.0894 EndY=-177.338 EndZ=0
    g77: LineSegment StartX=154.479 StartY=-146.678 StartZ=0 EndX=154.645 EndY=-146.747 EndZ=0
    g78: LineSegment StartX=130.229 StartY=-138.306 StartZ=0 EndX=128.529 EndY=-138.26 EndZ=0
    g79: LineSegment StartX=58.412 StartY=-172.055 StartZ=0 EndX=58.4951 EndY=-172.235 EndZ=0
    g80: LineSegment StartX=107.528 StartY=-141.563 StartZ=0 EndX=106.172 EndY=-142.257 EndZ=0
    g81: LineSegment StartX=72.3169 StartY=-177.021 StartZ=0 EndX=72.383 EndY=-176.906 EndZ=0
    g82: LineSegment StartX=115.741 StartY=-130.425 StartZ=0 EndX=115.741 EndY=-135.187 EndZ=0
    g83: LineSegment StartX=69.8513 StartY=-178.265 StartZ=0 EndX=69.978 EndY=-178.273 EndZ=0
    g84: LineSegment StartX=187.524 StartY=-145.256 StartZ=0 EndX=187.524 EndY=-138.113 EndZ=0
    g85: LineSegment StartX=70.8457 StartY=-178.16 StartZ=0 EndX=70.9642 EndY=-178.121 EndZ=0
    g86: LineSegment StartX=211.336 StartY=-145.256 StartZ=0 EndX=211.336 EndY=-141.684 EndZ=0
    g87: LineSegment StartX=158.489 StartY=-145.921 StartZ=0 EndX=158.61 EndY=-145.791 EndZ=0
    g88: LineSegment StartX=79.5166 StartY=-165.86 StartZ=0 EndX=78.7611 EndY=-166.947 EndZ=0
    g89: LineSegment StartX=96.445 StartY=-148.359 StartZ=0 EndX=95.6573 EndY=-148.979 EndZ=0
    g90: LineSegment StartX=125.185 StartY=-138.241 StartZ=0 EndX=123.569 EndY=-138.265 EndZ=0
    g91: LineSegment StartX=138.936 StartY=-139.265 StartZ=0 EndX=137.959 EndY=-139.032 EndZ=0
    g92: LineSegment StartX=91.1301 StartY=-153.066 StartZ=0 EndX=90.0477 EndY=-154.119 EndZ=0
    g93: LineSegment StartX=68.974 StartY=-178.03 StartZ=0 EndX=69.0967 EndY=-178.083 EndZ=0
    g94: LineSegment StartX=101.074 StartY=-145.221 StartZ=0 EndX=99.9796 EndY=-145.916 EndZ=0
    g95: LineSegment StartX=72.383 StartY=-176.906 StartZ=0 EndX=72.4439 EndY=-176.787 EndZ=0
    g96: LineSegment StartX=141.094 StartY=-139.926 StartZ=0 EndX=139.977 EndY=-139.56 EndZ=0
    g97: LineSegment StartX=71.8227 StartY=-177.612 StartZ=0 EndX=71.9156 EndY=-177.525 EndZ=0
    g98: LineSegment StartX=157.506 StartY=-146.628 StartZ=0 EndX=157.659 EndY=-146.549 EndZ=0
    g99: LineSegment StartX=152.01 StartY=-145.247 StartZ=0 EndX=150.035 EndY=-144.127 EndZ=0
    g100: LineSegment StartX=70.1045 StartY=-178.275 StartZ=0 EndX=70.2305 EndY=-178.27 EndZ=0
    g101: LineSegment StartX=71.0807 StartY=-178.076 StartZ=0 EndX=71.1951 EndY=-178.025 EndZ=0
    g102: LineSegment StartX=58.2195 StartY=-171.489 StartZ=0 EndX=58.2738 EndY=-171.681 EndZ=0
    g103: LineSegment StartX=155.67 StartY=-146.98 StartZ=0 EndX=155.843 EndY=-146.989 EndZ=0
    g104: LineSegment StartX=148.219 StartY=-143.142 StartZ=0 EndX=146.549 EndY=-142.284 EndZ=0
    g105: LineSegment StartX=90.0477 StartY=-154.119 StartZ=0 EndX=88.9357 EndY=-155.218 EndZ=0
    g106: LineSegment StartX=88.9357 StartY=-155.218 StartZ=0 EndX=86.6948 EndY=-157.481 EndZ=0
    g107: LineSegment StartX=92.2735 StartY=-53.5782 StartZ=0 EndX=91.0829 EndY=-53.5782 EndZ=0
    g108: LineSegment StartX=98.9895 StartY=-146.561 StartZ=0 EndX=98.0867 EndY=-147.17 EndZ=0
    g109: LineSegment StartX=115.21 StartY=-138.921 StartZ=0 EndX=114.589 EndY=-139.04 EndZ=0
    g110: LineSegment StartX=157.659 StartY=-146.549 StartZ=0 EndX=157.808 EndY=-146.463 EndZ=0
    g111: LineSegment StartX=117.762 StartY=-138.574 StartZ=0 EndX=116.468 EndY=-138.724 EndZ=0
    g112: LineSegment StartX=114.589 StartY=-139.04 StartZ=0 EndX=113.97 EndY=-139.174 EndZ=0
    g113: LineSegment StartX=58.1191 StartY=-170.903 StartZ=0 EndX=58.1422 EndY=-171.099 EndZ=0
    g114: LineSegment StartX=133.615 StartY=-138.475 StartZ=0 EndX=131.929 EndY=-138.377 EndZ=0
    g115: LineSegment StartX=137.717 StartY=-135.187 StartZ=0 EndX=137.717 EndY=-130.425 EndZ=0
    g116: LineSegment StartX=113.97 StartY=-139.174 StartZ=0 EndX=113.352 EndY=-139.324 EndZ=0
    g117: LineSegment StartX=158.61 StartY=-145.791 StartZ=0 EndX=158.725 EndY=-145.654 EndZ=0
    g118: LineSegment StartX=80.21 StartY=-164.893 StartZ=0 EndX=79.5166 EndY=-165.86 EndZ=0
    g119: LineSegment StartX=156.697 StartY=-146.908 StartZ=0 EndX=156.864 EndY=-146.868 EndZ=0
    g120: LineSegment StartX=86.6948 StartY=-157.481 StartZ=0 EndX=84.5514 EndY=-159.708 EndZ=0
    g121: LineSegment StartX=154.153 StartY=-146.511 StartZ=0 EndX=152.01 EndY=-145.247 EndZ=0
    g122: LineSegment StartX=70.2305 StartY=-178.27 StartZ=0 EndX=70.3558 EndY=-178.26 EndZ=0
    g123: LineSegment StartX=83.046 StartY=-161.339 StartZ=0 EndX=82.5343 EndY=-161.928 EndZ=0
    g124: LineSegment StartX=83.547 StartY=-160.783 StartZ=0 EndX=83.046 EndY=-161.339 EndZ=0
    g125: LineSegment StartX=84.5514 StartY=-159.708 StartZ=0 EndX=83.547 EndY=-160.783 EndZ=0
    g126: LineSegment StartX=155.843 StartY=-146.989 StartZ=0 EndX=156.016 EndY=-146.989 EndZ=0
    g127: LineSegment StartX=154.983 StartY=-146.86 StartZ=0 EndX=155.153 EndY=-146.903 EndZ=0
    g128: LineSegment StartX=157.19 StartY=-146.764 StartZ=0 EndX=157.349 EndY=-146.7 EndZ=0
    g129: LineSegment StartX=112.11 StartY=-139.678 StartZ=0 EndX=111.481 EndY=-139.884 EndZ=0
    g130: LineSegment StartX=157.953 StartY=-146.369 StartZ=0 EndX=158.094 EndY=-146.268 EndZ=0
    g131: LineSegment StartX=111.481 StartY=-139.884 StartZ=0 EndX=110.845 EndY=-140.111 EndZ=0
    g132: LineSegment StartX=183.952 StartY=-134.541 StartZ=0 EndX=168.474 EndY=-134.541 EndZ=0
    g133: LineSegment StartX=154.645 StartY=-146.747 StartZ=0 EndX=154.813 EndY=-146.808 EndZ=0
    g134: LineSegment StartX=94.0261 StartY=-150.367 StartZ=0 EndX=93.1338 EndY=-151.175 EndZ=0
    g135: LineSegment StartX=59.7759 StartY=-173.701 StartZ=0 EndX=59.9431 EndY=-173.807 EndZ=0
    g136: LineSegment StartX=72.0894 StartY=-177.338 StartZ=0 EndX=72.1698 EndY=-177.237 EndZ=0
    g137: LineSegment StartX=102.26 StartY=-144.49 StartZ=0 EndX=101.074 EndY=-145.221 EndZ=0
    g138: LineSegment StartX=145.013 StartY=-141.542 StartZ=0 EndX=143.6 EndY=-140.908 EndZ=0
    g139: LineSegment StartX=109.543 StartY=-140.632 StartZ=0 EndX=108.877 EndY=-140.924 EndZ=0
    g140: LineSegment StartX=137.033 StartY=-138.852 StartZ=0 EndX=135.291 EndY=-138.613 EndZ=0
    g141: LineSegment StartX=60.2955 StartY=-173.994 StartZ=0 EndX=68.974 EndY=-178.03 EndZ=0
    g142: LineSegment StartX=99.4173 StartY=-42.8625 StartZ=0 EndX=130.374 EndY=-42.8626 EndZ=0
    g143: LineSegment StartX=120.518 StartY=-138.376 StartZ=0 EndX=119.106 EndY=-138.461 EndZ=0
    g144: LineSegment StartX=58.4951 StartY=-172.235 StartZ=0 EndX=58.5871 EndY=-172.41 EndZ=0
    g145: LineSegment StartX=82.0035 StartY=-162.563 StartZ=0 EndX=81.4449 EndY=-163.259 EndZ=0
    g146: LineSegment StartX=69.4714 StartY=-178.203 StartZ=0 EndX=69.5977 EndY=-178.23 EndZ=0
    g147: LineSegment StartX=111.318 StartY=-131.65 StartZ=0 EndX=113.56 EndY=-135.848 EndZ=0
    g148: LineSegment StartX=137.959 StartY=-139.032 StartZ=0 EndX=137.033 EndY=-138.852 EndZ=0
    g149: LineSegment StartX=78.7611 StartY=-166.947 StartZ=0 EndX=77.9349 EndY=-168.167 EndZ=0
    g150: LineSegment StartX=218.48 StartY=-32.7422 StartZ=0 EndX=218.48 EndY=-134.541 EndZ=0
    g151: LineSegment StartX=158.094 StartY=-146.268 StartZ=0 EndX=158.231 EndY=-146.159 EndZ=0
    g152: LineSegment StartX=70.9642 StartY=-178.121 StartZ=0 EndX=71.0807 EndY=-178.076 EndZ=0
    g153: LineSegment StartX=110.199 StartY=-140.36 StartZ=0 EndX=109.543 EndY=-140.632 EndZ=0
    g154: LineSegment StartX=112.733 StartY=-139.492 StartZ=0 EndX=112.11 EndY=-139.678 EndZ=0
    g155: LineSegment StartX=157.028 StartY=-146.82 StartZ=0 EndX=157.19 EndY=-146.764 EndZ=0
    g156: LineSegment StartX=158.834 StartY=-145.511 StartZ=0 EndX=158.937 EndY=-145.361 EndZ=0
    g157: LineSegment StartX=69.978 StartY=-178.273 StartZ=0 EndX=70.1045 EndY=-178.275 EndZ=0
    g158: LineSegment StartX=119.106 StartY=-138.461 StartZ=0 EndX=117.762 EndY=-138.574 EndZ=0
    g159: LineSegment StartX=143.6 StartY=-140.908 StartZ=0 EndX=142.297 EndY=-140.372 EndZ=0
    g160: LineSegment StartX=95.8454 StartY=-50.0062 StartZ=0 EndX=95.8454 EndY=-46.4344 EndZ=0
    g161: LineSegment StartX=104.829 StartY=-142.989 StartZ=0 EndX=103.518 EndY=-143.739 EndZ=0
    g162: LineSegment StartX=71.4163 StartY=-177.908 StartZ=0 EndX=71.5227 EndY=-177.842 EndZ=0
    g163: LineSegment StartX=69.3457 StartY=-178.17 StartZ=0 EndX=69.4714 EndY=-178.203 EndZ=0
    g164: LineSegment StartX=58.2738 StartY=-171.681 StartZ=0 EndX=58.3381 EndY=-171.871 EndZ=0
    g165: LineSegment StartX=156.188 StartY=-146.981 StartZ=0 EndX=156.359 EndY=-146.965 EndZ=0
    g166: LineSegment StartX=158.937 StartY=-145.361 StartZ=0 EndX=159.033 EndY=-145.204 EndZ=0
    g167: LineSegment StartX=113.352 StartY=-139.324 StartZ=0 EndX=112.733 EndY=-139.492 EndZ=0
    g168: LineSegment StartX=135.291 StartY=-138.613 StartZ=0 EndX=133.615 EndY=-138.475 EndZ=0
    g169: LineSegment StartX=77.0295 StartY=-169.536 StartZ=0 EndX=76.0363 EndY=-171.068 EndZ=0
    g170: LineSegment StartX=58.1757 StartY=-171.295 StartZ=0 EndX=58.2195 EndY=-171.489 EndZ=0
    g171: LineSegment StartX=58.1422 StartY=-171.099 StartZ=0 EndX=58.1757 EndY=-171.295 EndZ=0
    g172: LineSegment StartX=137.517 StartY=-35.7188 StartZ=0 EndX=177.999 EndY=-35.7188 EndZ=0
    g173: LineSegment StartX=58.1111 StartY=-170.313 StartZ=0 EndX=58.1036 EndY=-170.51 EndZ=0
    g174: LineSegment StartX=58.5871 StartY=-172.41 StartZ=0 EndX=58.6879 EndY=-172.58 EndZ=0
    g175: LineSegment StartX=95.6573 StartY=-148.979 StartZ=0 EndX=94.8591 EndY=-149.641 EndZ=0
    g176: LineSegment StartX=87.511 StartY=-57.15 StartZ=0 EndX=87.511 EndY=-110.133 EndZ=0
    g177: LineSegment StartX=139.899 StartY=-135.848 StartZ=0 EndX=142.14 EndY=-131.65 EndZ=0
    g178: LineSegment StartX=71.626 StartY=-177.771 StartZ=0 EndX=71.7261 EndY=-177.694 EndZ=0
    g179: LineSegment StartX=98.0867 StartY=-147.17 StartZ=0 EndX=97.2466 EndY=-147.763 EndZ=0
    g180: ArcOfCircle CenterX=214.908 CenterY=-134.541 CenterZ=0 NormalX=0 NormalY=0 NormalZ=-1 AngleXU=-3.14158 Radius=3.57189 StartAngle=0 EndAngle=1.57078
    g181: ArcOfCircle CenterX=138.908 CenterY=-135.187 CenterZ=0 NormalX=0 NormalY=0 NormalZ=-1 AngleXU=-2.55359 Radius=1.19063 StartAngle=0 EndAngle=2.55359
    g182: ArcOfCircle CenterX=191.095 CenterY=-145.256 CenterZ=0 NormalX=0 NormalY=0 NormalZ=-1 AngleXU=-1.57084 Radius=3.57177 StartAngle=0 EndAngle=1.57087
    g183: ArcOfCircle CenterX=83.9387 CenterY=-110.133 CenterZ=0 NormalX=0 NormalY=0 NormalZ=-1 AngleXU=-3.14154 Radius=3.5723 StartAngle=0 EndAngle=0.785301
    g184: ArcOfCircle CenterX=177.999 CenterY=-33.9328 CenterZ=0 NormalX=0 NormalY=0 NormalZ=-1 AngleXU=-3.14159 Radius=1.78599 StartAngle=5.43116e-05 EndAngle=1.57076
    g185: ArcOfCircle CenterX=214.908 CenterY=-141.685 CenterZ=0 NormalX=0 NormalY=0 NormalZ=-1 AngleXU=6.10736e-06 Radius=3.57195 StartAngle=0 EndAngle=1.57077
    g186: ArcOfCircle CenterX=183.952 CenterY=-138.113 CenterZ=0 NormalX=0 NormalY=0 NormalZ=-1 AngleXU=1.57079 Radius=3.57192 StartAngle=0 EndAngle=1.57079
    g187: ArcOfCircle CenterX=113.36 CenterY=-130.425 CenterZ=0 NormalX=0 NormalY=0 NormalZ=-1 AngleXU=-0.540421 Radius=2.38125 StartAngle=0 EndAngle=3.68201
    g188: ArcOfCircle CenterX=183.356 CenterY=-33.9328 CenterZ=0 NormalX=0 NormalY=0 NormalZ=-1 AngleXU=-3.40383e-05 Radius=3.57182 StartAngle=4.47954e-06 EndAngle=1.57085
    g189: ArcOfCircle CenterX=140.099 CenterY=-130.425 CenterZ=0 NormalX=0 NormalY=0 NormalZ=-1 AngleXU=5.56759e-08 Radius=2.38125 StartAngle=0 EndAngle=3.68201
    g190: ArcOfCircle CenterX=91.0829 CenterY=-57.15 CenterZ=0 NormalX=0 NormalY=0 NormalZ=-1 AngleXU=-7.97628e-06 Radius=3.57185 StartAngle=0 EndAngle=1.57081
    g191: ArcOfCircle CenterX=65.4333 CenterY=-133.788 CenterZ=0 NormalX=0 NormalY=0 NormalZ=-1 AngleXU=0.104388 Radius=4.13372 StartAngle=0 EndAngle=0.867563
    g192: ArcOfCircle CenterX=168.474 CenterY=-137.887 CenterZ=0 NormalX=0 NormalY=0 NormalZ=-1 AngleXU=0.523599 Radius=3.3458 StartAngle=0 EndAngle=1.0472
    g193: ArcOfCircle CenterX=114.55 CenterY=-135.187 CenterZ=0 NormalX=0 NormalY=0 NormalZ=-1 AngleXU=3.14159 Radius=1.19063 StartAngle=0 EndAngle=2.55359
    g194: ArcOfCircle CenterX=99.4172 CenterY=-46.4343 CenterZ=0 NormalX=0 NormalY=0 NormalZ=-1 AngleXU=-3.49942e-05 Radius=3.5718 StartAngle=0 EndAngle=1.57085
    g195: ArcOfCircle CenterX=216.099 CenterY=-32.7422 CenterZ=0 NormalX=0 NormalY=0 NormalZ=-1 AngleXU=1.5708 Radius=2.38131 StartAngle=0 EndAngle=1.57078
    g196: ArcOfCircle CenterX=137.517 CenterY=-39.2906 CenterZ=0 NormalX=0 NormalY=0 NormalZ=-1 AngleXU=-2.73475e-05 Radius=3.57183 StartAngle=0 EndAngle=1.57084
    g197: ArcOfCircle CenterX=92.2736 CenterY=-50.0063 CenterZ=0 NormalX=0 NormalY=0 NormalZ=-1 AngleXU=3.14157 Radius=3.57184 StartAngle=0 EndAngle=1.57083
    g198: ArcOfCircle CenterX=130.374 CenterY=-39.2909 CenterZ=0 NormalX=0 NormalY=0 NormalZ=-1 AngleXU=3.14155 Radius=3.57176 StartAngle=0 EndAngle=1.57088
    g199: ArcOfCircle CenterX=207.764 CenterY=-145.256 CenterZ=0 NormalX=0 NormalY=0 NormalZ=-1 AngleXU=3.14156 Radius=3.57183 StartAngle=0 EndAngle=1.57084
    g200: Circle CenterX=194.667 CenterY=-39.886 CenterZ=0 NormalX=0 NormalY=0 NormalZ=1 AngleXU=0 Radius=4.16719
  constraints (200):
    c: Coincident(g42,g55)
    c: Coincident(g55,g173)
    c: Coincident(g42,g113)
    c: Coincident(g45,g173)
    c: Coincident(g24,g45)
    c: Coincident(g113,g171)
    c: Coincident(g24,g52)
    c: Coincident(g170,g171)
    c: Coincident(g102,g170)
    c: Coincident(g102,g164)
    c: Coincident(g72,g164)
    c: Coincident(g72,g79)
    c: Coincident(g79,g144)
    c: Coincident(g144,g174)
    c: Coincident(g34,g174)
    c: Coincident(g27,g34)
    c: Coincident(g27,g57)
    c: Coincident(g3,g57)
    c: Coincident(g3,g53)
    c: Coincident(g30,g53)
    c: Coincident(g30,g48)
    c: Coincident(g48,g50)
    c: Coincident(g50,g135)
    c: Coincident(g8,g135)
    c: Coincident(g8,g21)
    c: Coincident(g21,g141)
    c: Coincident(g52,g191)
    c: Coincident(g28,g191)
    c: Coincident(g93,g141)
    c: Coincident(g47,g93)
    c: Coincident(g22,g47)
    c: Coincident(g22,g163)
    c: Coincident(g146,g163)
    c: Coincident(g60,g146)
    c: Coincident(g9,g60)
    c: Coincident(g9,g83)
    c: Coincident(g83,g157)
    c: Coincident(g100,g157)
    c: Coincident(g100,g122)
    c: Coincident(g0,g122)
    c: Coincident(g0,g26)
    c: Coincident(g6,g26)
    c: Coincident(g6,g54)
    c: Coincident(g54,g85)
    c: Coincident(g85,g152)
    c: Coincident(g101,g152)
    c: Coincident(g75,g101)
    c: Coincident(g43,g75)
    c: Coincident(g43,g162)
    c: Coincident(g29,g162)
    c: Coincident(g29,g178)
    c: Coincident(g33,g178)
    c: Coincident(g33,g97)
    c: Coincident(g41,g97)
    c: Coincident(g41,g76)
    c: Coincident(g76,g136)
    c: Coincident(g68,g136)
    c: Coincident(g56,g68)
    c: Coincident(g56,g81)
    c: Coincident(g81,g95)
    c: Coincident(g62,g95)
    c: Coincident(g39,g62)
    c: Coincident(g36,g39)
    c: Coincident(g36,g169)
    c: Coincident(g12,g169)
    c: Coincident(g12,g149)
    c: Coincident(g88,g149)
    c: Coincident(g88,g118)
    c: Coincident(g40,g118)
    c: Coincident(g40,g65)
    c: Coincident(g65,g145)
    c: Coincident(g70,g145)
    c: Coincident(g70,g123)
    c: Coincident(g123,g124)
    c: Coincident(g124,g125)
    c: Coincident(g120,g125)
    c: Coincident(g28,g183)
    c: Coincident(g106,g120)
    c: Coincident(g176,g183)
    c: Coincident(g176,g190)
    c: Coincident(g105,g106)
    c: Coincident(g92,g105)
    c: Coincident(g107,g190)
    c: Coincident(g1,g92)
    c: Coincident(g1,g14)
    c: Coincident(g107,g197)
    c: Coincident(g14,g134)
    c: Coincident(g59,g134)
    c: Coincident(g59,g175)
    c: Coincident(g89,g175)
    c: Coincident(g160,g197)
    c: Coincident(g160,g194)
    c: Coincident(g11,g89)
    c: Coincident(g11,g179)
    c: Coincident(g108,g179)
    c: Coincident(g37,g108)
    c: Coincident(g142,g194)
    c: Coincident(g37,g94)
    c: Coincident(g94,g137)
    c: Coincident(g66,g137)
    c: Coincident(g66,g161)
    c: Coincident(g15,g161)
    c: Coincident(g15,g80)
    c: Coincident(g23,g80)
    c: Coincident(g23,g139)
    c: Coincident(g139,g153)
    c: Coincident(g38,g153)
    c: Coincident(g38,g131)
    c: Coincident(g147,g187)
    c: Coincident(g129,g131)
    c: Coincident(g129,g154)
    c: Coincident(g154,g167)
    c: Coincident(g116,g167)
    c: Coincident(g147,g193)
    c: Coincident(g112,g116)
    c: Coincident(g109,g112)
    c: Coincident(g17,g109)
    c: Coincident(g82,g193)
    c: Coincident(g82,g187)
    c: Coincident(g17,g111)
    c: Coincident(g111,g158)
    c: Coincident(g143,g158)
    c: Coincident(g5,g143)
    c: Coincident(g5,g13)
    c: Coincident(g13,g90)
    c: Coincident(g49,g90)
    c: Coincident(g49,g51)
    c: Coincident(g51,g78)
    c: Coincident(g18,g78)
    c: Coincident(g142,g198)
    c: Coincident(g18,g114)
    c: Coincident(g114,g168)
    c: Coincident(g196,g198)
    c: Coincident(g140,g168)
    c: Coincident(g140,g148)
    c: Coincident(g172,g196)
    c: Coincident(g115,g181)
    c: Coincident(g115,g189)
    c: Coincident(g91,g148)
    c: Coincident(g31,g91)
    c: Coincident(g177,g181)
    c: Coincident(g31,g96)
    c: Coincident(g46,g96)
    c: Coincident(g177,g189)
    c: Coincident(g46,g159)
    c: Coincident(g138,g159)
    c: Coincident(g7,g138)
    c: Coincident(g7,g104)
    c: Coincident(g63,g104)
    c: Coincident(g63,g99)
    c: Coincident(g99,g121)
    c: Coincident(g44,g121)
    c: Coincident(g20,g44)
    c: Coincident(g20,g77)
    c: Coincident(g77,g133)
    c: Coincident(g2,g133)
    c: Coincident(g2,g127)
    c: Coincident(g35,g127)
    c: Coincident(g16,g35)
    c: Coincident(g10,g16)
    c: Coincident(g10,g103)
    c: Coincident(g103,g126)
    c: Coincident(g64,g126)
    c: Coincident(g64,g165)
    c: Coincident(g69,g165)
    c: Coincident(g32,g69)
    c: Coincident(g32,g119)
    c: Coincident(g71,g119)
    c: Coincident(g71,g155)
    c: Coincident(g128,g155)
    c: Coincident(g4,g128)
    c: Coincident(g4,g98)
    c: Coincident(g98,g110)
    c: Coincident(g19,g110)
    c: Coincident(g19,g130)
    c: Coincident(g130,g151)
    c: Coincident(g61,g151)
    c: Coincident(g61,g67)
    c: Coincident(g67,g87)
    c: Coincident(g87,g117)
    c: Coincident(g74,g117)
    c: Coincident(g74,g156)
    c: Coincident(g156,g166)
    c: Coincident(g58,g166)
    c: Coincident(g58,g192)
    c: Coincident(g132,g192)
    c: Coincident(g172,g184)
    c: Coincident(g184,g188)
    c: Coincident(g25,g188)
    c: Coincident(g132,g186)
    c: Coincident(g84,g182)
    c: Coincident(g84,g186)
    c: Coincident(g73,g182)
    c: Coincident(g73,g199)
    c: Coincident(g86,g199)
    c: Coincident(g86,g185)
    c: Coincident(g180,g185)
    c: Coincident(g25,g195)
    c: Coincident(g150,g180)
    c: Coincident(g150,g195)
FEATURE [App::Part] Board_Geoms_ed69
  Group = -> [Pcb_ed69,PCB_Sketch_ed69]
  Origin = -> Origin007
FEATURE [App::Part] Step_Models_ed69
  Origin = -> Origin008
FEATURE [App::Part] Board_ed69  label="mykeeb_v7a3-base"
  Group = -> [Local_CS_ed69,Board_Geoms_ed69,Step_Models_ed69]
  Origin = -> Origin006
  Placement = pos=(0,0,-3) rot=(0,0,1;0rad)
